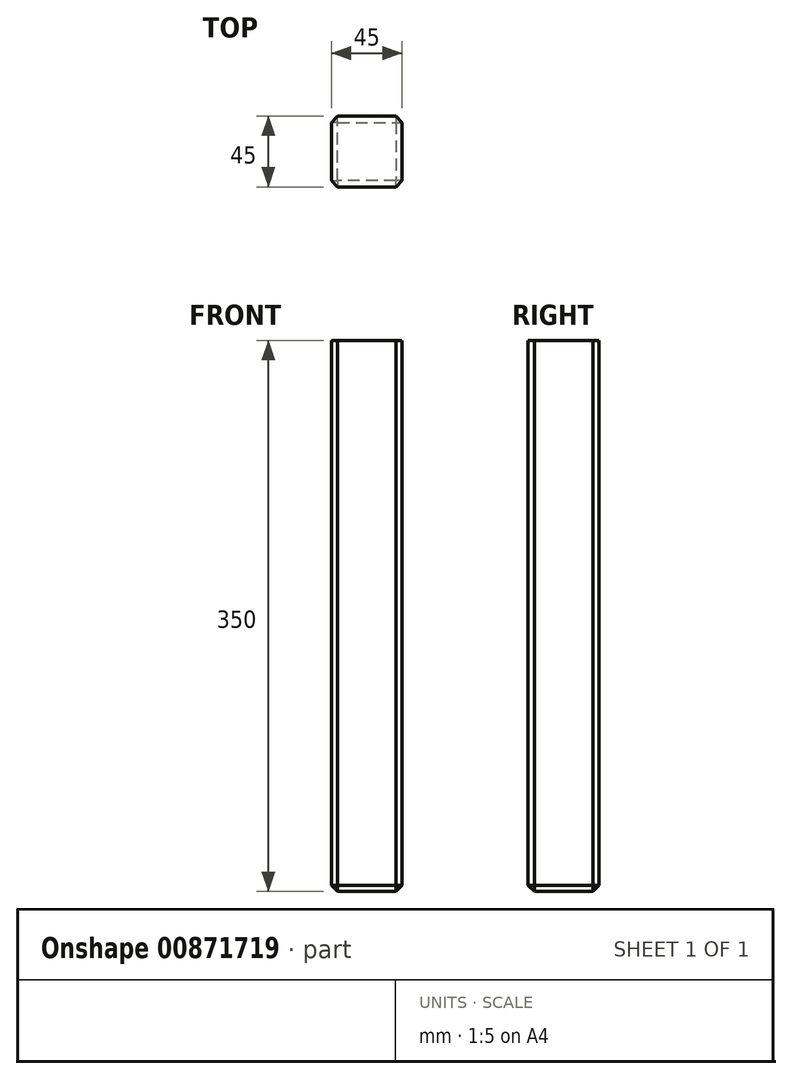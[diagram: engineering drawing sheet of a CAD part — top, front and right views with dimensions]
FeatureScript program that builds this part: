
annotation { "Feature Type Name" : "Feature", "Feature Type Description" : "" }
export const myFeature = defineFeature(function(context is Context, id is Id, definition is map)
    precondition{}
    {
        {
            var Q0;
            Q0=qCreatedBy(makeId("Front.planeOp"),FACE);
            var sketch = newSketch(context, id + "F0", { "sketchPlane" : qUnion([Q0])});
            skLineSegment(sketch, "E0.bottom", {"start": v(0, 0) * mm, "end": v(45, 0) * mm});
            skLineSegment(sketch, "E0.top", {"start": v(0, 350) * mm, "end": v(45, 350) * mm});
            skLineSegment(sketch, "E0.left", {"start": v(0, 0) * mm, "end": v(0, 350) * mm});
            skLineSegment(sketch, "E0.right", {"start": v(45, 0) * mm, "end": v(45, 350) * mm});
            skSolve(sketch);
        }
        {
            var Q0;
            Q0=makeQuery(id+"F0.imprint","IMPRINT",FACE,{"disambiguationData":[TD([[makeQuery(id+"F0.imprint","IMPRINT",EDGE,{"derivedFrom":sQuery(id+"F0.wireOp",EDGE,"E0.bottom")}),1.0]])]});
            extrude(context, id + "F1", {"entities" : qUnion([Q0]), "depth" : 45 * mm, "offsetDistance" : 25 * mm});
        }
        {
            var Q0;
            Q0=makeQuery(id+"F1.opExtrude","CAP_EDGE",EDGE,{"disambiguationData":[OSD([sQuery(id+"F0.wireOp",EDGE,"E0.left")])],"isStart":false});
            var Q1;
            Q1=makeQuery(id+"F1.opExtrude","CAP_EDGE",EDGE,{"disambiguationData":[OSD([sQuery(id+"F0.wireOp",EDGE,"E0.right")])],"isStart":false});
            var Q2;
            Q2=makeQuery(id+"F1.opExtrude","CAP_EDGE",EDGE,{"disambiguationData":[OSD([sQuery(id+"F0.wireOp",EDGE,"E0.right")])],"isStart":true});
            var Q3;
            Q3=makeQuery(id+"F1.opExtrude","CAP_EDGE",EDGE,{"disambiguationData":[OSD([sQuery(id+"F0.wireOp",EDGE,"E0.left")])],"isStart":true});
            var Q4;
            Q4=makeQuery(id+"F1.opExtrude","SWEPT_EDGE",EDGE,{"disambiguationData":[OSD([sQuery(id+"F0.wireOp",EDGE,"E0.bottom"),sQuery(id+"F0.wireOp",EDGE,"E0.right")])]});
            var Q5;
            Q5=makeQuery(id+"F1.opExtrude","CAP_EDGE",EDGE,{"disambiguationData":[OSD([sQuery(id+"F0.wireOp",EDGE,"E0.bottom")])],"isStart":true});
            var Q6;
            Q6=makeQuery(id+"F1.opExtrude","SWEPT_EDGE",EDGE,{"disambiguationData":[OSD([sQuery(id+"F0.wireOp",EDGE,"E0.bottom"),sQuery(id+"F0.wireOp",EDGE,"E0.left")])]});
            var Q7;
            Q7=makeQuery(id+"F1.opExtrude","CAP_EDGE",EDGE,{"disambiguationData":[OSD([sQuery(id+"F0.wireOp",EDGE,"E0.bottom")])],"isStart":false});
            chamfer(context, id + "F2", {"entities" : qUnion([Q0, Q1, Q2, Q3, Q4, Q5, Q6, Q7]), "width" : 4 * mm, "tangentPropagation" : true});
        }
    });
